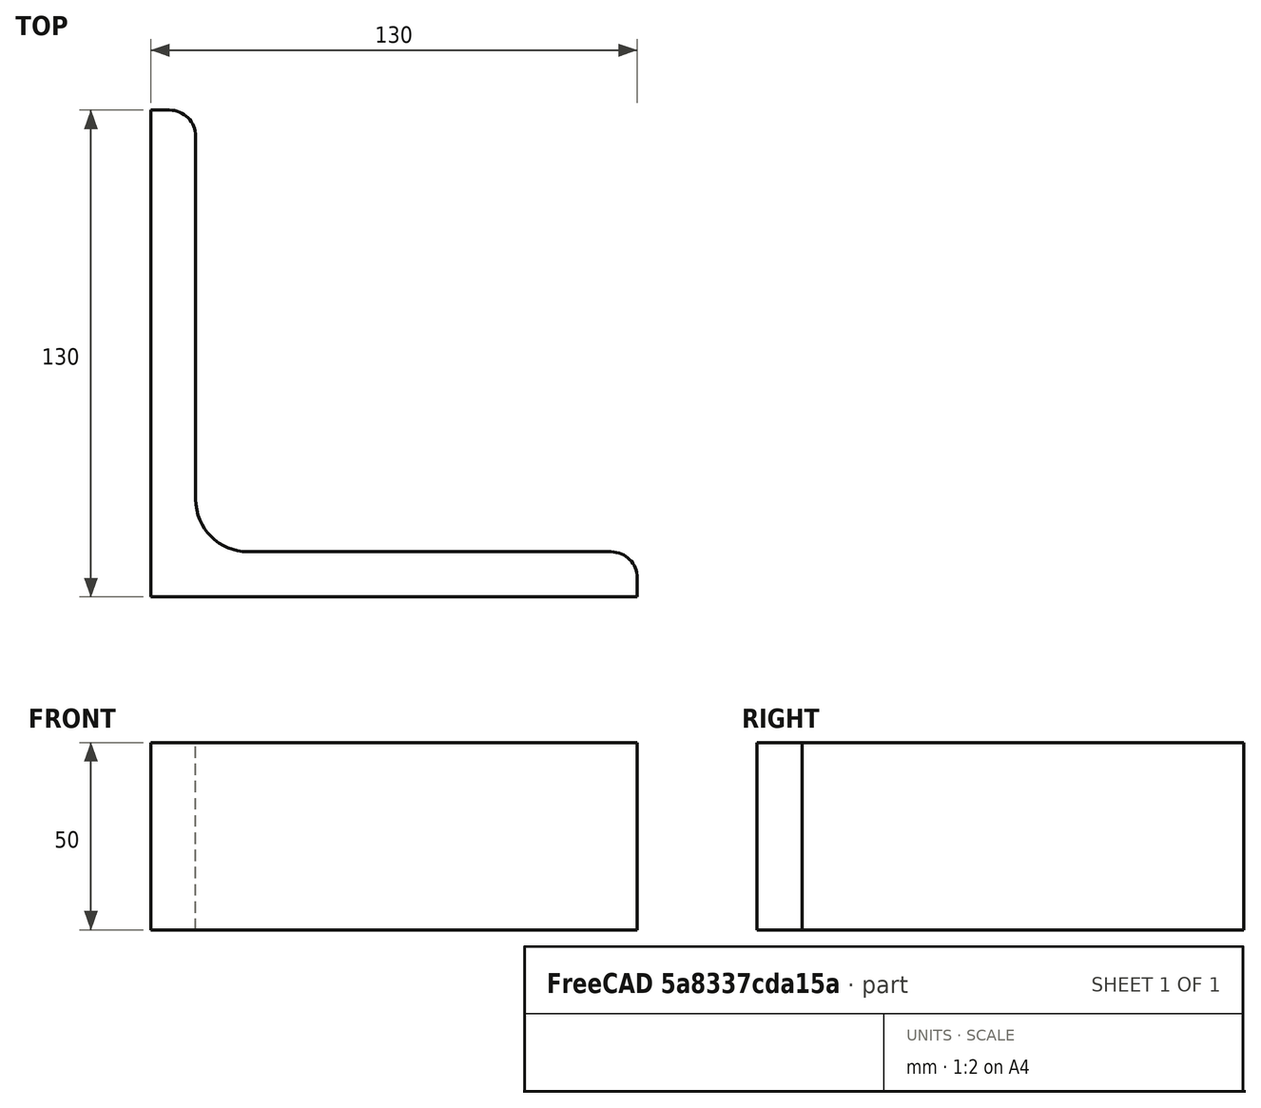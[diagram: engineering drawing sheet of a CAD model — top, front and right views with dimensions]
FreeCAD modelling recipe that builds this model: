
FCSTD DOCUMENT  (FreeCAD 0.15R4671 (Git))
Label: Angle Bar L130x130x12 EN10056 S235JR
License: All rights reserved
LicenseURL: http://en.wikipedia.org/wiki/All_rights_reserved
objects: Sketcher::SketchObject×1, Part::Extrusion×1
note: 2 computed .brp shape members not serialized (recipe doc carries the construction recipe); baked Part::Feature solids carry a one-line shape summary decoded from their .brp

FEATURE [Sketcher::SketchObject] Sketch
  sketch-geometry (9):
    g0: LineSegment StartX=0 StartY=0 StartZ=0 EndX=130 EndY=0 EndZ=0
    g1: LineSegment StartX=130 StartY=0 StartZ=0 EndX=130 EndY=5 EndZ=0
    g2: LineSegment StartX=123 StartY=12 StartZ=0 EndX=26 EndY=12 EndZ=0
    g3: LineSegment StartX=0 StartY=0 StartZ=0 EndX=0 EndY=130 EndZ=0
    g4: LineSegment StartX=0 StartY=130 StartZ=0 EndX=5 EndY=130 EndZ=0
    g5: LineSegment StartX=12 StartY=123 StartZ=0 EndX=12 EndY=26 EndZ=0
    g6: ArcOfCircle CenterX=26 CenterY=26 CenterZ=0 NormalX=0 NormalY=0 NormalZ=1 Radius=14 StartAngle=3.14159 EndAngle=4.71239
    g7: ArcOfCircle CenterX=5 CenterY=123 CenterZ=0 NormalX=0 NormalY=0 NormalZ=1 Radius=7 StartAngle=0 EndAngle=1.5708
    g8: ArcOfCircle CenterX=123 CenterY=5 CenterZ=0 NormalX=0 NormalY=0 NormalZ=1 Radius=7 StartAngle=0 EndAngle=1.5708
  constraints (23):
    c: Coincident(g0,g-1)
    c: Horizontal(g0)
    c: Coincident(g1,g0)
    c: Vertical(g1)
    c: Horizontal(g2)
    c: Coincident(g3,g-1)
    c: Vertical(g3)
    c: Coincident(g4,g3)
    c: Horizontal(g4)
    c: Vertical(g5)
    c: Tangent(g5,g6) = -1.5708
    c: Tangent(g2,g6) = 1.5708
    c: Tangent(g4,g7) = 1.5708
    c: Tangent(g5,g7) = 1.5708
    c: Tangent(g2,g8) = -1.5708
    c: Tangent(g1,g8) = -1.5708
    c: DistanceX(g0) = 130
    c: DistanceY(g3) = 130
    c: DistanceY(g0,g2) = 12
    c: DistanceX(g3,g5) = 12
    c: Radius(g6) = 14
    c: Radius(g8) = 7
    c: Radius(g7) = 7
FEATURE [Part::Extrusion] Extrude  label="Angle Bar L130x130x12 EN10056 S235JR"
  Base = -> Sketch
  Dir = (0,0,50)
  Solid = true
